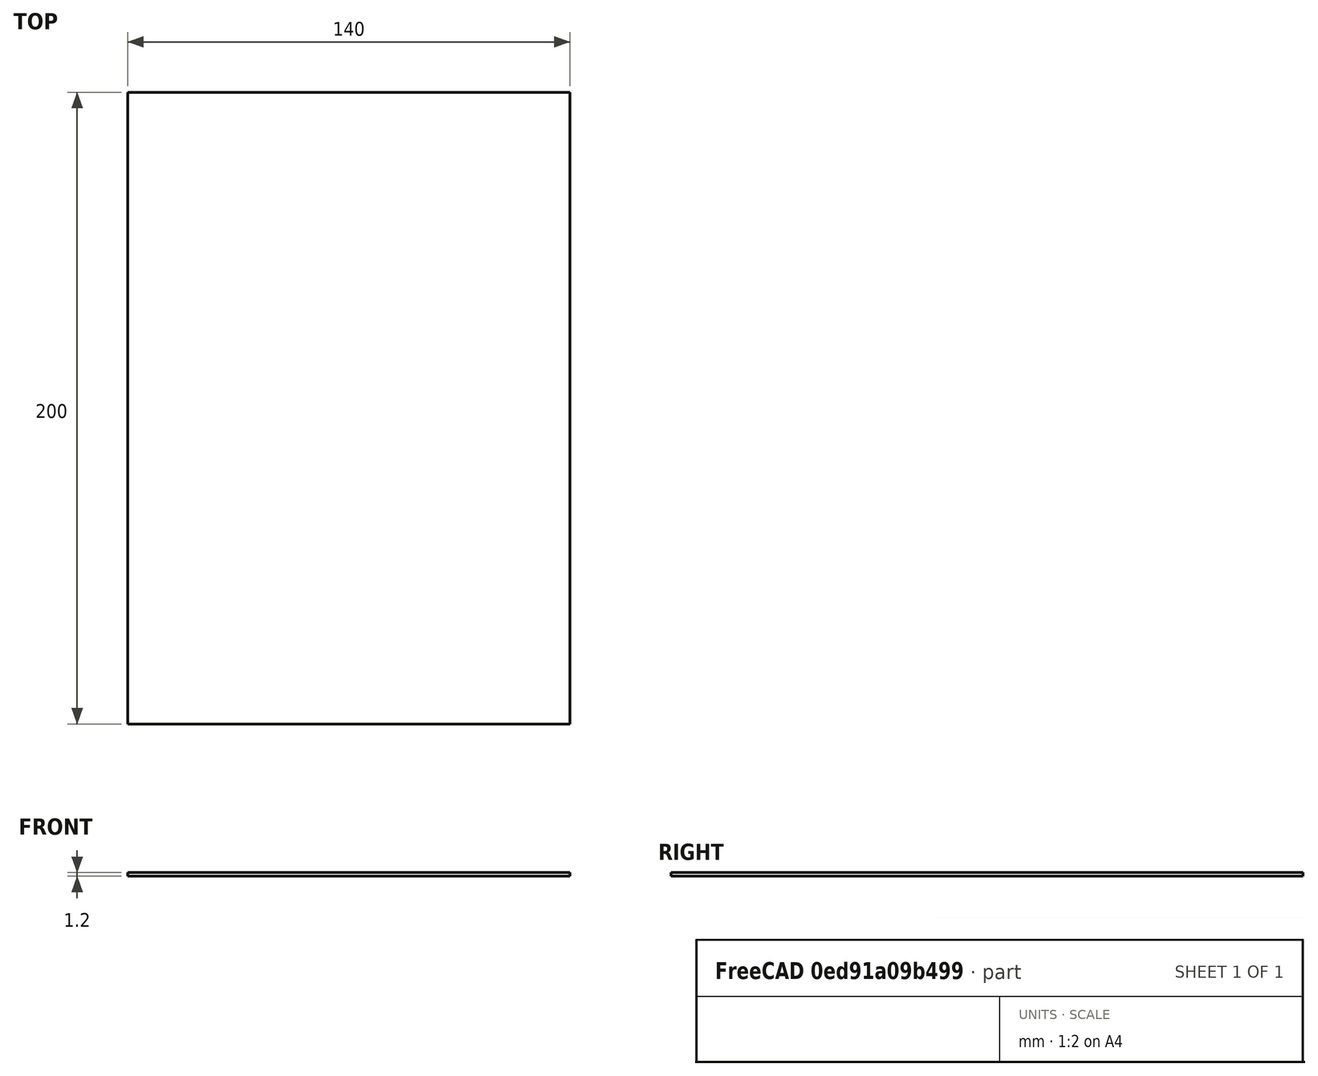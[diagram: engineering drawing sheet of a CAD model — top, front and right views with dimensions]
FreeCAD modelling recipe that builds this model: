
FCSTD DOCUMENT  (FreeCAD 0.20R29603 (Git))
Label: Digit_80x80_Base
License: All rights reserved
LicenseURL: http://en.wikipedia.org/wiki/All_rights_reserved
objects: Sketcher::SketchObject×1, PartDesign::Pad×1, PartDesign::Body×1
note: 4 computed .brp shape members not serialized (recipe doc carries the construction recipe); baked Part::Feature solids carry a one-line shape summary decoded from their .brp

FEATURE [Sketcher::SketchObject] Sketch
  FullyConstrained = true
  MapMode = 5
  Support = -> [XY_Plane]
  sketch-geometry (4):
    g0: LineSegment StartX=-70 StartY=100 StartZ=0 EndX=70 EndY=100 EndZ=0
    g1: LineSegment StartX=70 StartY=100 StartZ=0 EndX=70 EndY=-100 EndZ=0
    g2: LineSegment StartX=70 StartY=-100 StartZ=0 EndX=-70 EndY=-100 EndZ=0
    g3: LineSegment StartX=-70 StartY=-100 StartZ=0 EndX=-70 EndY=100 EndZ=0
  constraints (10):
    c: Coincident(g0,g1)
    c: Coincident(g1,g2)
    c: Coincident(g2,g3)
    c: Coincident(g3,g0)
    c: Horizontal(g2)
    c: Vertical(g1)
    c: Symmetric(g0,g2,g-1)
    c: Symmetric(g0,g0,g-2)
    c: DistanceX(g2,g2) = 140
    c: DistanceY(g2,g0) = 200
FEATURE [PartDesign::Pad] Pad
  Direction = (0,0,1)
  Length = 1.2
  Length2 = 10
  Profile = -> Sketch
  ReferenceAxis = -> Sketch [N_Axis]
  Type = 0
FEATURE [PartDesign::Body] Body
  Group = -> [Sketch,Pad]
  Origin = -> Origin
  Tip = -> Pad
